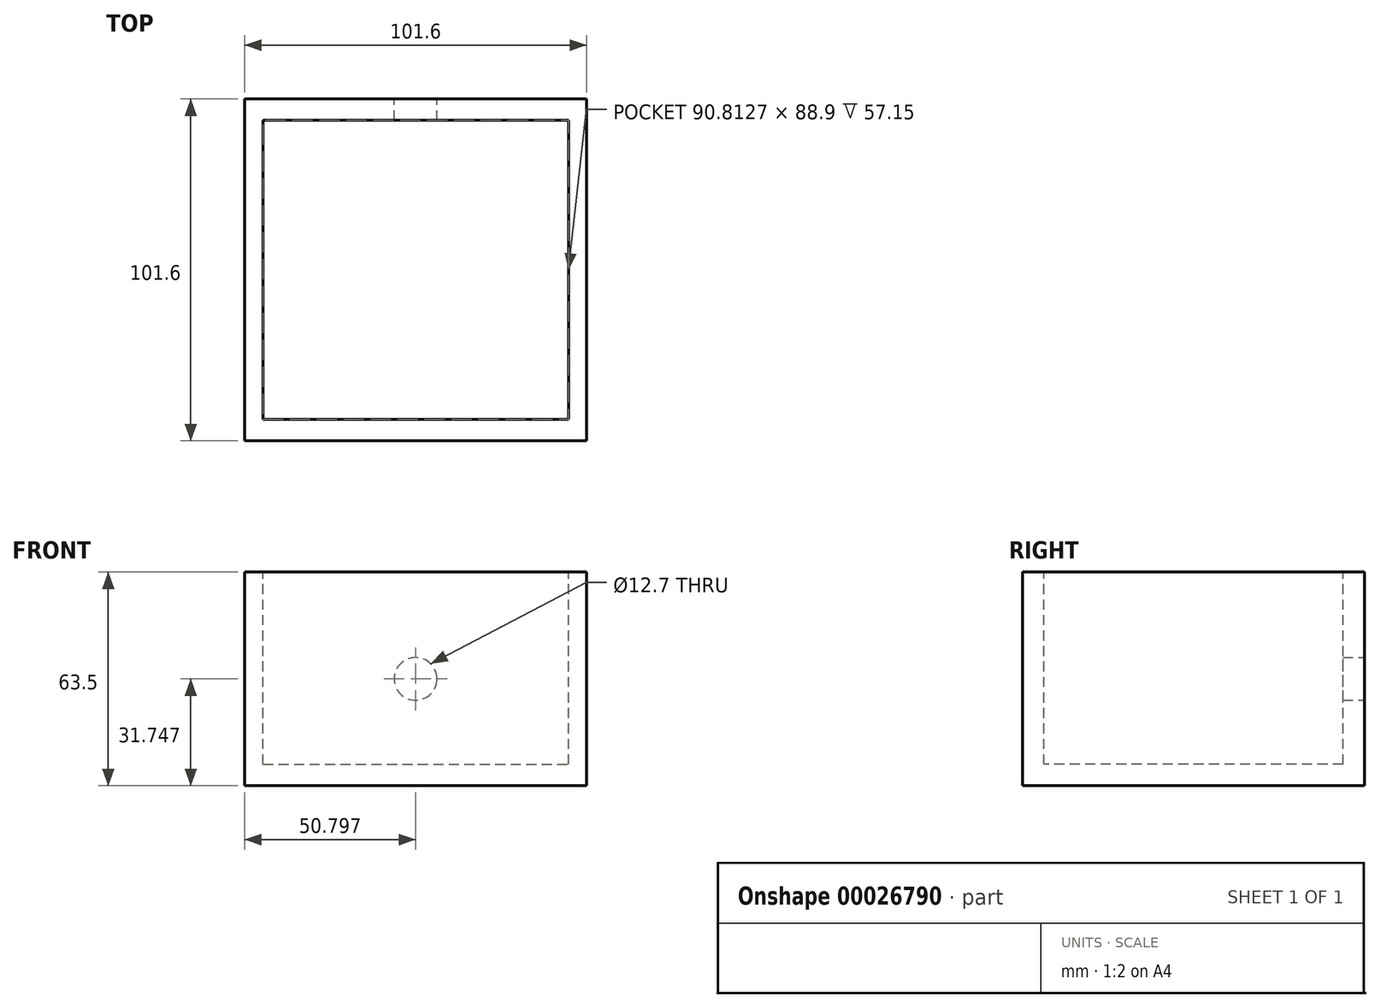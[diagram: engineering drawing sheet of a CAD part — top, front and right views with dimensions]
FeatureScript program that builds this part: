
annotation { "Feature Type Name" : "Feature", "Feature Type Description" : "" }
export const myFeature = defineFeature(function(context is Context, id is Id, definition is map)
    precondition{}
    {
        {
            var Q0;
            Q0=qCreatedBy(makeId("Front.planeOp"),FACE);
            var sketch = newSketch(context, id + "F0", { "sketchPlane" : qUnion([Q0])});
            skLineSegment(sketch, "E0.bottom", {"start": v(-46.76, 31.64) * mm, "end": v(54.84, 31.64) * mm});
            skLineSegment(sketch, "E0.top", {"start": v(-46.76, -31.86) * mm, "end": v(54.84, -31.86) * mm});
            skLineSegment(sketch, "E0.left", {"start": v(-46.76, 31.64) * mm, "end": v(-46.76, -31.86) * mm});
            skLineSegment(sketch, "E0.right", {"start": v(54.84, 31.64) * mm, "end": v(54.84, -31.86) * mm});
            skCircle(sketch, "E1", {"center": v(4.04, -0.11) * mm, "radius": 6.35 * mm});
            skPoint(sketch, "E2.orphan", {"position": v(4.04, 31.64) * mm});
            skPoint(sketch, "E3.orphan", {"position": v(-46.76, -0.11) * mm});
            skSolve(sketch);
        }
        {
            var Q0;
            Q0=makeQuery(id+"F0.imprint","IMPRINT",FACE,{"disambiguationData":[TD([[makeQuery(id+"F0.imprint","IMPRINT",EDGE,{"derivedFrom":sQuery(id+"F0.wireOp",EDGE,"E0.bottom")}),-1.0]])]});
            var Q1;
            Q1=makeQuery(id+"F0.imprint","IMPRINT",FACE,{"disambiguationData":[TD([[makeQuery(id+"F0.imprint","IMPRINT",EDGE,{"derivedFrom":sQuery(id+"F0.wireOp",EDGE,"E1")}),1.0]])]});
            extrude(context, id + "F1", {"entities" : qUnion([Q0, Q1]), "depth" : 101.6 * mm});
        }
        {
            var Q0;
            Q0=makeQuery(id+"F0.imprint","IMPRINT",FACE,{"disambiguationData":[TD([[makeQuery(id+"F0.imprint","IMPRINT",EDGE,{"derivedFrom":sQuery(id+"F0.wireOp",EDGE,"E1")}),1.0]])]});
            extrude(context, id + "F2", {"entities" : qUnion([Q0]), "operationType" : NewBodyOperationType.REMOVE, "depth" : 25.4 * mm});
        }
        {
            var Q0;
            Q0=makeQuery(id+"F1.opExtrude","SWEPT_FACE",FACE,{"disambiguationData":[OSD([sQuery(id+"F0.wireOp",EDGE,"E0.bottom")])]});
            var sketch = newSketch(context, id + "F3", { "sketchPlane" : qUnion([Q0])});
            skLineSegment(sketch, "E4.bottom", {"start": v(-41.27, -6.35) * mm, "end": v(49.54, -6.35) * mm});
            skLineSegment(sketch, "E4.top", {"start": v(-41.27, -95.25) * mm, "end": v(49.54, -95.25) * mm});
            skLineSegment(sketch, "E4.left", {"start": v(-41.27, -6.35) * mm, "end": v(-41.27, -95.25) * mm});
            skLineSegment(sketch, "E4.right", {"start": v(49.54, -6.35) * mm, "end": v(49.54, -95.25) * mm});
            skSolve(sketch);
        }
        {
            var Q0;
            Q0=makeQuery(id+"F3.imprint","IMPRINT",FACE,{"disambiguationData":[TD([[makeQuery(id+"F3.imprint","IMPRINT",EDGE,{"derivedFrom":sQuery(id+"F3.wireOp",EDGE,"E4.bottom")}),-1.0]])]});
            extrude(context, id + "F4", {"entities" : qUnion([Q0]), "operationType" : NewBodyOperationType.REMOVE, "oppositeDirection" : true, "depth" : 57.15 * mm});
        }
    });
